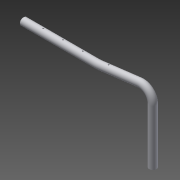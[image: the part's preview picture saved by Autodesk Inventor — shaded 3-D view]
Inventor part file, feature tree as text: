
AUTODESK INVENTOR PART (.ipt)
format: ipt  version: 2015 (Build 190159000, 159)  size: 190,464 bytes
history: native  units: mm
features: sketch x5, other x4, extrude x2, shell x1
ambient origin geometry x8: Origin, YZ Plane, XZ Plane, XY Plane, X Axis, Y Axis, Z Axis, Center Point
bodies: Body1 (feature_tree)
feature tree (12):
  other  "Bryła1"
  extrude  "Wyciągnięcie proste1"  Depth=32.0mm
  shell  "Skorupa1"  Thickness=815.0mm
  other  "Gięcie części1"
  sketch  "Szkic7"
  other  "Płaszczyzna konstrukcyjna4"
  other  "Gięcie części2"
  extrude  "Wyciągnięcie proste3"  Depth=2.0mm
  sketch  "Szkic1"
  sketch  "Szkic4"
  sketch  "Szkic8"
  sketch  "Szkic9"
